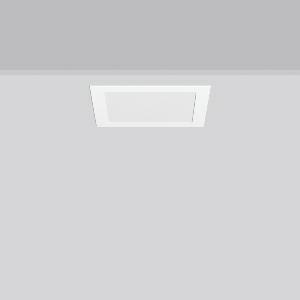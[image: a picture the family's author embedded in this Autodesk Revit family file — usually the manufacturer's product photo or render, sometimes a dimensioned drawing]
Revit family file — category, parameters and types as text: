
# Revit family: toledo_flat_square_e_901670_002_730_51d1
name_source: partatom
category: Lighting Fixtures
units: mm (PartAtom-declared; Revit-internal decimal feet)

## family parameters
Cut with Voids When Loaded = No
Host = Face
Light Source = No
Part Type = Normal
Room Calculation Point = No
Round Connector Dimension = Use Diameter
Shared = No

## types (1)
- TuneableWhite 846 (1 x LED Modul 846, 1600 lm, 4600)
    Apparent Load = 19 VA
    CIE Flux Codes = 48 79 96 100 100
    Color Rendering = 80
    Color Temperature = 4600
    Default Elevation = 1800 mm
    Description = Series: TOLEDO FLAT square
Ultra thin recessed downlight. Housing: die-cast aluminium. Light guide and diffuser made of non-yellowing PMMA, opal matt. Tunable white dynamically adjustable from 2700 K to 6500 K.With Casambi smart+free Bluetooth control for wireless network and operation using Android / iOS devices, free app available for download. Ceiling installation with spring system. Mounting depth depends on ceiling strength. Surface mounted housing as accessory for all sizes. Retrofittable decorative cylinders made of chintz fabric as accessory, optional with satin finish plastic diffuser. Through-wiring box (5 pole) available as accessory. 
Colour: white
Length: 225 mm
Width: 225 mm
Height: 3 mm
Cut-out length: 208 mm
Cut-out width: 208 mm
Recess height: 55-75 mm
Luminaire: recess height: 31-51 mm
Lamp: LED
Socket: without socket
Colour temperature: 2700K - 6500K
Colour rendering index (CRI): 80
System power: 19 W
Rated luminous flux: 1600 lm
Luminous efficiency: 84 lm/W
System power 2: 20 W
Rated luminous flux 2: 1500 lm
Luminous efficiency 2: 75 lm/W
System power 3: 18 W
Rated luminous flux 3: 1550 lm
Luminous efficiency 3: 86 lm/W
Control gear: Dimmable Bluetooth converter
Protection class: II
Type of protection: IP 54
    Height = 0 mm  [stored 0 ft]
    Lamp = 1 x LED Modul 846
    Lamp Light Flux = 1600 lm
    Lamp count = 1
    Length = 225 mm
    Lifetime = 50000 h
    Luminous efficacy = 84 lm/W
    Manufacturer = RZB
    ModVariant = No
    Model = 901670.002.730
    Mounting Place = Ceiling
    Mounting Type = Recessed
    Number of Poles = 1
    OnlyDefault = Yes
    Power Factor = 1
    Product Name = TOLEDO FLAT square E
    Product group = Recessed downlights
    ProductGroupID = 402
    Protection Class = Protection class II
    Protection Degree = IP 40
    RLX_Detail_Level = 1
    RLX_Emergency_Light_Flux = 0 lm
    RLX_Emergency_Type = 0
    RLX_Emergency_Type_DB = No
    RlxData = <blob elided: 58557 chars, md5=a1f7bfe9>
    Socket = socket
    Standby Power = 0 W
    System Light Flux = 1600 lm
    System Power = 19 W
    Type Comments = TuneableWhite 846
    Type Image = 901487.002.jpg
    URL = http://relux.com
    VarID = tuneablewhite_846
    Voltage = 230 V
    Voltage Range = 220-240 V
    Weight = 0.00 kg
    Width = 225 mm

note: [stored X ft] marks values corroborated as IEEE doubles in the binary element streams (Revit-internal decimal feet)

## geometry (parser evidence)
native form markers: Blend x4, Sweep x9
no freeform markers — native parametric forms only
